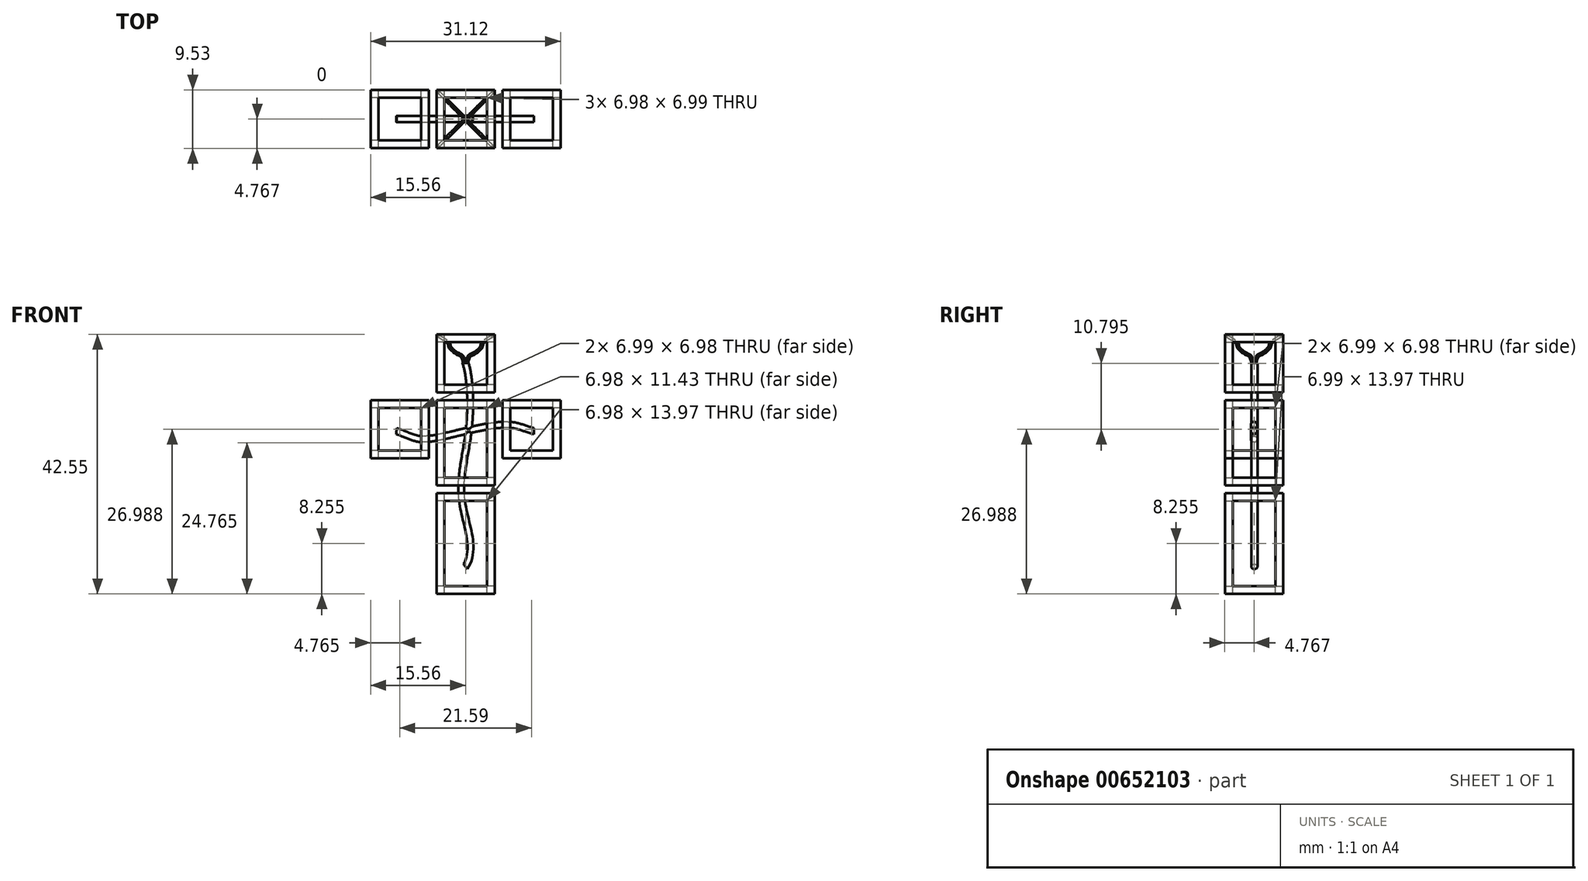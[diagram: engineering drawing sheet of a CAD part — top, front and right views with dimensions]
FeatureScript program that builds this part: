
annotation { "Feature Type Name" : "Feature", "Feature Type Description" : "" }
export const myFeature = defineFeature(function(context is Context, id is Id, definition is map)
    precondition{}
    {
        {
            var Q0;
            Q0=qCreatedBy(makeId("Front.planeOp"),FACE);
            var sketch = newSketch(context, id + "F0", { "sketchPlane" : qUnion([Q0])});
            skLineSegment(sketch, "E0.bottom", {"start": v(-4.73, 15.87) * mm, "end": v(4.8, 15.87) * mm});
            skLineSegment(sketch, "E0.top", {"start": v(-4.73, 6.34) * mm, "end": v(4.8, 6.34) * mm});
            skLineSegment(sketch, "E0.left", {"start": v(-4.73, 15.87) * mm, "end": v(-4.73, 6.34) * mm});
            skLineSegment(sketch, "E0.right", {"start": v(4.8, 15.87) * mm, "end": v(4.8, 6.34) * mm});
            skLineSegment(sketch, "E1.bottom", {"start": v(-15.53, 5.07) * mm, "end": v(-6, 5.07) * mm});
            skLineSegment(sketch, "E1.top", {"start": v(-15.53, -4.45) * mm, "end": v(-6, -4.45) * mm});
            skLineSegment(sketch, "E1.left", {"start": v(-15.53, 5.07) * mm, "end": v(-15.53, -4.45) * mm});
            skLineSegment(sketch, "E1.right", {"start": v(-6, 5.07) * mm, "end": v(-6, -4.45) * mm});
            skLineSegment(sketch, "E2.bottom", {"start": v(6.06, 5.07) * mm, "end": v(15.59, 5.07) * mm});
            skLineSegment(sketch, "E2.top", {"start": v(6.06, -4.45) * mm, "end": v(15.59, -4.45) * mm});
            skLineSegment(sketch, "E2.left", {"start": v(6.06, 5.07) * mm, "end": v(6.06, -4.45) * mm});
            skLineSegment(sketch, "E2.right", {"start": v(15.59, 5.07) * mm, "end": v(15.59, -4.45) * mm});
            skLineSegment(sketch, "E3.bottom", {"start": v(-4.73, 5.07) * mm, "end": v(4.8, 5.07) * mm});
            skLineSegment(sketch, "E3.top", {"start": v(-4.73, -8.9) * mm, "end": v(4.8, -8.9) * mm});
            skLineSegment(sketch, "E3.left", {"start": v(-4.73, 5.07) * mm, "end": v(-4.73, -8.9) * mm});
            skLineSegment(sketch, "E3.right", {"start": v(4.8, 5.07) * mm, "end": v(4.8, -8.9) * mm});
            skLineSegment(sketch, "E4.bottom", {"start": v(-4.73, -10.17) * mm, "end": v(4.8, -10.17) * mm});
            skLineSegment(sketch, "E4.top", {"start": v(-4.73, -26.68) * mm, "end": v(4.8, -26.68) * mm});
            skLineSegment(sketch, "E4.left", {"start": v(-4.73, -10.17) * mm, "end": v(-4.73, -26.68) * mm});
            skLineSegment(sketch, "E4.right", {"start": v(4.8, -10.17) * mm, "end": v(4.8, -26.68) * mm});
            skSolve(sketch);
        }
        {
            var Q0;
            Q0=makeQuery(id+"F0.imprint","IMPRINT",FACE,{"disambiguationData":[TD([[makeQuery(id+"F0.imprint","IMPRINT",EDGE,{"derivedFrom":sQuery(id+"F0.wireOp",EDGE,"E0.bottom")}),-1.0]])]});
            var Q1;
            Q1=makeQuery(id+"F0.imprint","IMPRINT",FACE,{"disambiguationData":[TD([[makeQuery(id+"F0.imprint","IMPRINT",EDGE,{"derivedFrom":sQuery(id+"F0.wireOp",EDGE,"E1.bottom")}),-1.0]])]});
            var Q2;
            Q2=makeQuery(id+"F0.imprint","IMPRINT",FACE,{"disambiguationData":[TD([[makeQuery(id+"F0.imprint","IMPRINT",EDGE,{"derivedFrom":sQuery(id+"F0.wireOp",EDGE,"E2.bottom")}),-1.0]])]});
            var Q3;
            Q3=makeQuery(id+"F0.imprint","IMPRINT",FACE,{"disambiguationData":[TD([[makeQuery(id+"F0.imprint","IMPRINT",EDGE,{"derivedFrom":sQuery(id+"F0.wireOp",EDGE,"E3.bottom")}),-1.0]])]});
            var Q4;
            Q4=makeQuery(id+"F0.imprint","IMPRINT",FACE,{"disambiguationData":[TD([[makeQuery(id+"F0.imprint","IMPRINT",EDGE,{"derivedFrom":sQuery(id+"F0.wireOp",EDGE,"E4.bottom")}),-1.0]])]});
            extrude(context, id + "F1", {"entities" : qUnion([Q0, Q1, Q2, Q3, Q4]), "depth" : 9.52 * mm, "offsetDistance" : 25.4 * mm});
        }
        {
            var Q0;
            Q0=makeQuery(id+"F1.opExtrude","CAP_FACE",FACE,{"disambiguationData":[OSD([sQuery(id+"F0.wireOp",EDGE,"E0.bottom"),sQuery(id+"F0.wireOp",EDGE,"E0.top"),sQuery(id+"F0.wireOp",EDGE,"E0.left"),sQuery(id+"F0.wireOp",EDGE,"E0.right")])],"isStart":true});
            var sketch = newSketch(context, id + "F2", { "sketchPlane" : qUnion([Q0])});
            skLineSegment(sketch, "E5.bottom", {"start": v(-3.52, 14.6) * mm, "end": v(3.46, 14.6) * mm});
            skLineSegment(sketch, "E5.top", {"start": v(-3.52, 7.61) * mm, "end": v(3.46, 7.61) * mm});
            skLineSegment(sketch, "E5.left", {"start": v(-3.52, 14.6) * mm, "end": v(-3.52, 7.61) * mm});
            skLineSegment(sketch, "E5.right", {"start": v(3.46, 14.6) * mm, "end": v(3.46, 7.61) * mm});
            skLineSegment(sketch, "E6.bottom", {"start": v(7.27, 3.8) * mm, "end": v(14.26, 3.8) * mm});
            skLineSegment(sketch, "E6.top", {"start": v(7.27, -3.18) * mm, "end": v(14.26, -3.18) * mm});
            skLineSegment(sketch, "E6.left", {"start": v(7.27, 3.8) * mm, "end": v(7.27, -3.18) * mm});
            skLineSegment(sketch, "E6.right", {"start": v(14.26, 3.8) * mm, "end": v(14.26, -3.18) * mm});
            skLineSegment(sketch, "E7.bottom", {"start": v(-14.32, 3.8) * mm, "end": v(-7.33, 3.8) * mm});
            skLineSegment(sketch, "E7.top", {"start": v(-14.32, -3.18) * mm, "end": v(-7.33, -3.18) * mm});
            skLineSegment(sketch, "E7.left", {"start": v(-14.32, 3.8) * mm, "end": v(-14.32, -3.18) * mm});
            skLineSegment(sketch, "E7.right", {"start": v(-7.33, 3.8) * mm, "end": v(-7.33, -3.18) * mm});
            skLineSegment(sketch, "E8.bottom", {"start": v(-3.52, 3.8) * mm, "end": v(3.46, 3.8) * mm});
            skLineSegment(sketch, "E8.top", {"start": v(-3.52, -7.63) * mm, "end": v(3.46, -7.63) * mm});
            skLineSegment(sketch, "E8.left", {"start": v(-3.52, 3.8) * mm, "end": v(-3.52, -7.63) * mm});
            skLineSegment(sketch, "E8.right", {"start": v(3.46, 3.8) * mm, "end": v(3.46, -7.63) * mm});
            skLineSegment(sketch, "E9.bottom", {"start": v(-3.52, -11.44) * mm, "end": v(3.46, -11.44) * mm});
            skLineSegment(sketch, "E9.top", {"start": v(-3.52, -25.4) * mm, "end": v(3.46, -25.4) * mm});
            skLineSegment(sketch, "E9.left", {"start": v(-3.52, -11.44) * mm, "end": v(-3.52, -25.4) * mm});
            skLineSegment(sketch, "E9.right", {"start": v(3.46, -11.44) * mm, "end": v(3.46, -25.4) * mm});
            skSolve(sketch);
        }
        {
            var Q0;
            Q0 = qSketchRegion(id + "F2", true);
            extrude(context, id + "F3", {"entities" : qUnion([Q0]), "operationType" : NewBodyOperationType.REMOVE, "endBound" : BoundingType.THROUGH_ALL, "oppositeDirection" : true, "depth" : 25.4 * mm, "offsetDistance" : 25.4 * mm});
        }
        {
            var Q0;
            Q0=makeQuery(id+"F1.opExtrude","SWEPT_FACE",FACE,{"disambiguationData":[OSD([sQuery(id+"F0.wireOp",EDGE,"E0.bottom")])]});
            var sketch = newSketch(context, id + "F4", { "sketchPlane" : qUnion([Q0])});
            skLineSegment(sketch, "E10.bottom", {"start": v(-3.46, -1.27) * mm, "end": v(3.52, -1.27) * mm});
            skLineSegment(sketch, "E10.top", {"start": v(-3.46, -8.25) * mm, "end": v(3.52, -8.25) * mm});
            skLineSegment(sketch, "E10.left", {"start": v(-3.46, -1.27) * mm, "end": v(-3.46, -8.25) * mm});
            skLineSegment(sketch, "E10.right", {"start": v(3.52, -1.27) * mm, "end": v(3.52, -8.25) * mm});
            skLineSegment(sketch, "E11.bottom", {"start": v(7.33, -1.27) * mm, "end": v(14.32, -1.27) * mm});
            skLineSegment(sketch, "E11.top", {"start": v(7.33, -8.26) * mm, "end": v(14.32, -8.26) * mm});
            skLineSegment(sketch, "E11.left", {"start": v(7.33, -1.27) * mm, "end": v(7.33, -8.26) * mm});
            skLineSegment(sketch, "E11.right", {"start": v(14.32, -1.27) * mm, "end": v(14.32, -8.26) * mm});
            skLineSegment(sketch, "E12.bottom", {"start": v(-14.26, -1.27) * mm, "end": v(-7.27, -1.27) * mm});
            skLineSegment(sketch, "E12.top", {"start": v(-14.26, -8.26) * mm, "end": v(-7.27, -8.26) * mm});
            skLineSegment(sketch, "E12.left", {"start": v(-14.26, -1.27) * mm, "end": v(-14.26, -8.26) * mm});
            skLineSegment(sketch, "E12.right", {"start": v(-7.27, -1.27) * mm, "end": v(-7.27, -8.26) * mm});
            skSolve(sketch);
        }
        {
            var Q0;
            Q0 = qSketchRegion(id + "F4", true);
            extrude(context, id + "F5", {"entities" : qUnion([Q0]), "operationType" : NewBodyOperationType.REMOVE, "endBound" : BoundingType.THROUGH_ALL, "oppositeDirection" : true, "depth" : 25.4 * mm, "offsetDistance" : 25.4 * mm});
        }
        {
            var Q0;
            Q0=makeQuery(id+"F1.opExtrude","SWEPT_FACE",FACE,{"disambiguationData":[OSD([sQuery(id+"F0.wireOp",EDGE,"E1.left")])]});
            var sketch = newSketch(context, id + "F6", { "sketchPlane" : qUnion([Q0])});
            skLineSegment(sketch, "E13.bottom", {"start": v(1.27, 3.8) * mm, "end": v(8.26, 3.8) * mm});
            skLineSegment(sketch, "E13.top", {"start": v(1.27, -3.18) * mm, "end": v(8.26, -3.18) * mm});
            skLineSegment(sketch, "E13.left", {"start": v(1.27, 3.8) * mm, "end": v(1.27, -3.18) * mm});
            skLineSegment(sketch, "E13.right", {"start": v(8.26, 3.8) * mm, "end": v(8.26, -3.18) * mm});
            skLineSegment(sketch, "E14.bottom", {"start": v(1.27, 14.6) * mm, "end": v(8.25, 14.6) * mm});
            skLineSegment(sketch, "E14.top", {"start": v(1.27, 7.61) * mm, "end": v(8.25, 7.61) * mm});
            skLineSegment(sketch, "E14.left", {"start": v(1.27, 14.6) * mm, "end": v(1.27, 7.61) * mm});
            skLineSegment(sketch, "E14.right", {"start": v(8.25, 14.6) * mm, "end": v(8.25, 7.61) * mm});
            skLineSegment(sketch, "E15.bottom", {"start": v(1.27, -11.44) * mm, "end": v(8.26, -11.44) * mm});
            skLineSegment(sketch, "E15.top", {"start": v(1.27, -25.4) * mm, "end": v(8.26, -25.4) * mm});
            skLineSegment(sketch, "E15.left", {"start": v(1.27, -11.44) * mm, "end": v(1.27, -25.4) * mm});
            skLineSegment(sketch, "E15.right", {"start": v(8.26, -11.44) * mm, "end": v(8.26, -25.4) * mm});
            skSolve(sketch);
        }
        {
            var Q0;
            Q0 = qSketchRegion(id + "F6", true);
            extrude(context, id + "F7", {"entities" : qUnion([Q0]), "operationType" : NewBodyOperationType.REMOVE, "endBound" : BoundingType.THROUGH_ALL, "oppositeDirection" : true, "depth" : 25.4 * mm, "offsetDistance" : 25.4 * mm});
        }
        {
            var Q0;
            Q0=makeQuery(id+"F1.opExtrude","SWEPT_FACE",FACE,{"disambiguationData":[OSD([sQuery(id+"F0.wireOp",EDGE,"E3.left")])]});
            var sketch = newSketch(context, id + "F8", { "sketchPlane" : qUnion([Q0])});
            skLineSegment(sketch, "E16.bottom", {"start": v(1.27, 3.8) * mm, "end": v(8.25, 3.8) * mm});
            skLineSegment(sketch, "E16.top", {"start": v(1.27, -7.63) * mm, "end": v(8.26, -7.63) * mm});
            skLineSegment(sketch, "E16.left", {"start": v(1.27, 3.8) * mm, "end": v(1.27, -7.63) * mm});
            skLineSegment(sketch, "E16.right", {"start": v(8.26, 3.8) * mm, "end": v(8.26, -7.63) * mm});
            skSolve(sketch);
        }
        {
            var Q0;
            Q0 = qSketchRegion(id + "F8", true);
            extrude(context, id + "F9", {"entities" : qUnion([Q0]), "operationType" : NewBodyOperationType.REMOVE, "endBound" : BoundingType.THROUGH_ALL, "oppositeDirection" : true, "depth" : 25.4 * mm, "offsetDistance" : 25.4 * mm});
        }
        {
            var Q0;
            Q0=makeQuery(id+"F7.boolean.opBoolean","INTERSECT",EDGE,{"derivedFrom":[makeQuery(id+"F1.opExtrude","SWEPT_FACE",FACE,{"disambiguationData":[OSD([sQuery(id+"F0.wireOp",EDGE,"E0.right")])]}),makeQuery(id+"F7.opExtrude","SWEPT_FACE",FACE,{"disambiguationData":[OSD([sQuery(id+"F6.wireOp",EDGE,"E14.right")])]})]});
            cPoint(context, id + "F10", {"entities" : qUnion([Q0]), "parameter" : 0.5});
        }
        {
            var Q0;
            Q0=makeQuery(id+"F7.boolean.opBoolean","INTERSECT",EDGE,{"derivedFrom":[makeQuery(id+"F1.opExtrude","SWEPT_FACE",FACE,{"disambiguationData":[OSD([sQuery(id+"F0.wireOp",EDGE,"E0.right")])]}),makeQuery(id+"F7.opExtrude","SWEPT_FACE",FACE,{"disambiguationData":[OSD([sQuery(id+"F6.wireOp",EDGE,"E14.left")])]})]});
            cPoint(context, id + "F11", {"entities" : qUnion([Q0]), "parameter" : 0.5});
        }
        {
            var Q0;
            Q0 = qCreatedBy(id + "F10" ,VERTEX);
            var Q1;
            Q1 = qCreatedBy(id + "F11" ,VERTEX);
            cPlane(context, id + "F12", {"entities" : qUnion([Q0, Q1]), "cplaneType" : CPlaneType.MID_PLANE, "offset" : 25.4 * mm, "width" : 152.4 * mm, "height" : 152.4 * mm});
        }
        {
            var Q0;
            Q0=qCreatedBy(id+"F12.planeOp",FACE);
            var sketch = newSketch(context, id + "F13", { "sketchPlane" : qUnion([Q0])});
            skFitSpline(sketch, "E17", {"points": [v(0, 11.18) * mm, v(-0.74, 2.78) * mm, v(0, -3.44) * mm, v(0.7, -9.38) * mm, v(0, -14.25) * mm, v(-0.82, -18.7) * mm, v(0, -22.22) * mm], "startDerivative": vector(-10.13, -29.26) * mm, "endDerivative": vector(13.96, -21.11) * mm});
            skSolve(sketch);
        }
        {
            var Q0;
            Q0=makeQuery(id+"F3.boolean.opBoolean","INTERSECT",EDGE,{"derivedFrom":[makeQuery(id+"F1.opExtrude","CAP_FACE",FACE,{"disambiguationData":[OSD([sQuery(id+"F0.wireOp",EDGE,"E0.bottom"),sQuery(id+"F0.wireOp",EDGE,"E0.top"),sQuery(id+"F0.wireOp",EDGE,"E0.left"),sQuery(id+"F0.wireOp",EDGE,"E0.right")])],"isStart":false}),makeQuery(id+"F3.opExtrude","SWEPT_FACE",FACE,{"disambiguationData":[OSD([sQuery(id+"F2.wireOp",EDGE,"E5.right")])]})]});
            cPoint(context, id + "F14", {"entities" : qUnion([Q0]), "parameter" : 0.5});
        }
        {
            var Q0;
            Q0=makeQuery(id+"F3.boolean.opBoolean","INTERSECT",EDGE,{"derivedFrom":[makeQuery(id+"F1.opExtrude","CAP_FACE",FACE,{"disambiguationData":[OSD([sQuery(id+"F0.wireOp",EDGE,"E0.bottom"),sQuery(id+"F0.wireOp",EDGE,"E0.top"),sQuery(id+"F0.wireOp",EDGE,"E0.left"),sQuery(id+"F0.wireOp",EDGE,"E0.right")])],"isStart":false}),makeQuery(id+"F3.opExtrude","SWEPT_FACE",FACE,{"disambiguationData":[OSD([sQuery(id+"F2.wireOp",EDGE,"E5.left")])]})]});
            cPoint(context, id + "F15", {"entities" : qUnion([Q0]), "parameter" : 0.5});
        }
        {
            var Q0;
            Q0=sQuery(id+"F13.wireOp",VERTEX,"E17.0.internal");
            var Q1;
            Q1 = qCreatedBy(id + "F14" ,VERTEX);
            var Q2;
            Q2 = qCreatedBy(id + "F15" ,VERTEX);
            cPlane(context, id + "F16", {"entities" : qUnion([Q0, Q1, Q2]), "cplaneType" : CPlaneType.THREE_POINT, "offset" : 25.4 * mm, "width" : 152.4 * mm, "height" : 152.4 * mm});
        }
        {
            var Q0;
            Q0=qCreatedBy(id+"F16.planeOp",FACE);
            var sketch = newSketch(context, id + "F17", { "sketchPlane" : qUnion([Q0])});
            skCircle(sketch, "E18", {"center": v(0, 4.51) * mm, "radius": 0.5 * mm});
            skSolve(sketch);
        }
        {
            var Q0;
            Q0 = qSketchRegion(id + "F17", true);
            var Q1;
            Q1 = qConstructionFilter(qBodyType(qCreatedBy(id + "F13" ,EDGE), BodyType.WIRE), ConstructionObject.NO);
            sweep(context, id + "F18", {"profiles" : qUnion([Q0]), "path" : qUnion([Q1])});
        }
        {
            var Q0;
            Q0=qCreatedBy(id+"F12.planeOp",FACE);
            var sketch = newSketch(context, id + "F19", { "sketchPlane" : qUnion([Q0])});
            skFitSpline(sketch, "E19", {"points": [v(-11.21, 0) * mm, v(-7.31, 1.03) * mm, v(0, 0) * mm, v(7.26, -1.3) * mm, v(11.3, 0) * mm], "startDerivative": vector(23.08, 6.28) * mm, "endDerivative": vector(24.95, 8.61) * mm});
            skSolve(sketch);
        }
        {
            var Q0;
            Q0=qCreatedBy(makeId("Right.planeOp"),FACE);
            var Q1;
            Q1=sQuery(id+"F19.wireOp",VERTEX,"E19.start");
            cPlane(context, id + "F20", {"entities" : qUnion([Q0, Q1]), "cplaneType" : CPlaneType.PLANE_POINT, "offset" : 25.4 * mm, "width" : 152.4 * mm, "height" : 152.4 * mm});
        }
        {
            var Q0;
            Q0=qCreatedBy(id+"F20.planeOp",FACE);
            var sketch = newSketch(context, id + "F21", { "sketchPlane" : qUnion([Q0])});
            skCircle(sketch, "E20", {"center": v(-4.75, 0) * mm, "radius": 0.5 * mm});
            skSolve(sketch);
        }
        {
            var Q0;
            Q0 = qSketchRegion(id + "F21", true);
            var Q1;
            Q1 = qConstructionFilter(qBodyType(qCreatedBy(id + "F19" ,EDGE), BodyType.WIRE), ConstructionObject.NO);
            sweep(context, id + "F22", {"operationType" : NewBodyOperationType.ADD, "profiles" : qUnion([Q0]), "path" : qUnion([Q1])});
        }
        {
            var Q0;
            Q0=makeQuery(id+"F5.boolean.opBoolean","INTERSECT",VERTEX,{"derivedFrom":[makeQuery(id+"F1.opExtrude","SWEPT_FACE",FACE,{"disambiguationData":[OSD([sQuery(id+"F0.wireOp",EDGE,"E4.top")])]}),makeQuery(id+"F5.opExtrude","SWEPT_FACE",FACE,{"disambiguationData":[OSD([sQuery(id+"F4.wireOp",EDGE,"E10.bottom")])]}),makeQuery(id+"F5.opExtrude","SWEPT_FACE",FACE,{"disambiguationData":[OSD([sQuery(id+"F4.wireOp",EDGE,"E10.left")])]})]});
            var Q1;
            Q1=makeQuery(id+"F5.boolean.opBoolean","INTERSECT",VERTEX,{"derivedFrom":[makeQuery(id+"F1.opExtrude","SWEPT_FACE",FACE,{"disambiguationData":[OSD([sQuery(id+"F0.wireOp",EDGE,"E4.top")])]}),makeQuery(id+"F5.opExtrude","SWEPT_FACE",FACE,{"disambiguationData":[OSD([sQuery(id+"F4.wireOp",EDGE,"E10.top")])]}),makeQuery(id+"F5.opExtrude","SWEPT_FACE",FACE,{"disambiguationData":[OSD([sQuery(id+"F4.wireOp",EDGE,"E10.right")])]})]});
            cPlane(context, id + "F23", {"entities" : qUnion([Q0, Q1]), "cplaneType" : CPlaneType.MID_PLANE, "offset" : 25.4 * mm, "width" : 152.4 * mm, "height" : 152.4 * mm});
        }
        {
            var Q0;
            Q0=qCreatedBy(id+"F23.planeOp",FACE);
            var sketch = newSketch(context, id + "F24", { "sketchPlane" : qUnion([Q0])});
            skFitSpline(sketch, "E21", {"points": [v(-3.75, 11.26) * mm, v(-4.28, 12.2) * mm, v(-5.4, 12.66) * mm, v(-7.07, 13.75) * mm, v(-7.32, 14.32) * mm, v(-9.8, 15.55) * mm], "startDerivative": vector(-2.44, 6.31) * mm, "endDerivative": vector(-11.8, 4.57) * mm});
            skSolve(sketch);
        }
        {
            var Q0;
            Q0=qCreatedBy(id+"F16.planeOp",FACE);
            var sketch = newSketch(context, id + "F25", { "sketchPlane" : qUnion([Q0])});
            skCircle(sketch, "E22", {"center": v(-0.2, 4.77) * mm, "radius": 0.2 * mm});
            skSolve(sketch);
        }
        {
            var Q0;
            Q0 = qSketchRegion(id + "F25", true);
            var Q1;
            Q1 = qConstructionFilter(qBodyType(qCreatedBy(id + "F24" ,EDGE), BodyType.WIRE), ConstructionObject.NO);
            sweep(context, id + "F26", {"profiles" : qUnion([Q0]), "path" : qUnion([Q1])});
        }
        {
            var Q0;
            Q0=qCreatedBy(id+"F23.planeOp",FACE);
            var sketch = newSketch(context, id + "F27", { "sketchPlane" : qUnion([Q0])});
            skLineSegment(sketch, "E23", {"start": v(-3.36, 11.13) * mm, "end": v(-3.36, 13.89) * mm});
            skSolve(sketch);
        }
        {
            var Q0;
            Q0=makeQuery(id+"F26.opSweep","SWEPT_BODY",BODY,{"disambiguationData":[OSD([sQuery(id+"F24.wireOp",EDGE,"E21"),sQuery(id+"F25.wireOp",EDGE,"E22")])]});
            var Q1;
            Q1=sQuery(id+"F27.wireOp",EDGE,"E23");
            circularPattern(context, id + "F28", {"entities" : qUnion([Q0]), "axis" : qUnion([Q1]), "angle" : 360 * degree, "instanceCount" : 4, "equalSpace" : true});
        }
    });
